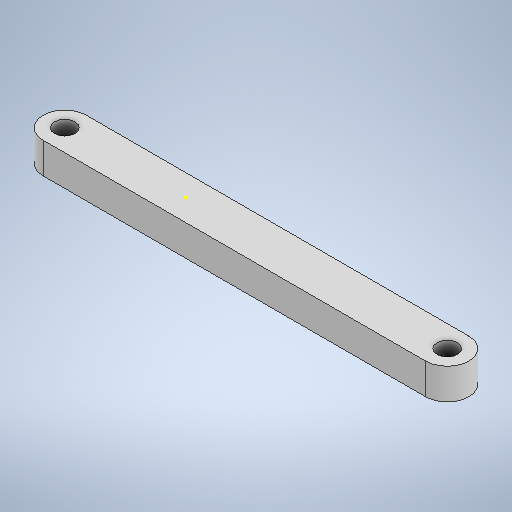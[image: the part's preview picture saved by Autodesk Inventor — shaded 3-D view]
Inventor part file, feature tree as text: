
AUTODESK INVENTOR PART (.ipt)
format: ipt  version: 2025.1 (Build 291241020, 241B)  size: 330,240 bytes
history: native  units: mm
features: sketch x7, extrude x4, move_body x4, boolean_combine x4, split x3, other x1, fillet x1, plane x1, imported_body x1
ambient origin geometry x8: Origin, YZ Plane, XZ Plane, XY Plane, X Axis, Y Axis, Z Axis, Center Point
bodies: Solid1 (feature_tree), Solid2 (feature_tree), Solid3 (feature_tree), Solid4 (feature_tree), Solid5 (feature_tree), Solid6 (feature_tree), Solid7 (feature_tree), Solid8 (feature_tree)
feature tree (26):
  other  "Repaired Geometry1"
  extrude  "Extrusion1"  Depth=7.0mm
  fillet  "Fillet1"  Radius=3.3mm
  move_body  "Move Body1"
  split  "Split1"
  move_body  "Move Body2"
  boolean_combine  "Combine1"
  sketch  "Sketch4"  dims[d5=3.5mm d6=5.0mm d7=0.0mm]
  plane  "Work Plane1"
  split  "Split2"
  split  "Split3"
  move_body  "Move Body3"
  move_body  "Move Body4"
  sketch  "Sketch5"  dims[d8=3.5mm d9=0.0mm d10=0.0mm d11=10.0mm]
  sketch  "Sketch6"  dims[d12=-0.1mm d13=0.0mm d14=0.0mm]
  extrude  "Extrusion2"  Depth=3.5mm
  extrude  "Extrusion3"  Depth=5.0mm TaperAngle=0.0deg
  boolean_combine  "Combine2"
  boolean_combine  "Combine3"
  sketch  "Sketch7"  dims[d15=2.0mm]
  boolean_combine  "Combine4"
  extrude  "Extrusion4"  Depth=10.0mm TaperAngle=0.0deg
  sketch  "Sketch1"  dims[d0=7.0mm d1=39.4mm d2=3.3mm]
  imported_body  "Base1"
  sketch  "Sketch2"  dims[d3=3.3mm d4=3.5mm]
  sketch  "Sketch8"  dims[d16=90.0deg d17=22.5mm d18=0.0mm d19=0.0mm d20=10.7mm d21=0.0mm d22=0.0mm d23=10.0mm d24=0.0mm d25=10.0mm d26=0.0mm d27=10.0mm d28=0.0mm]
